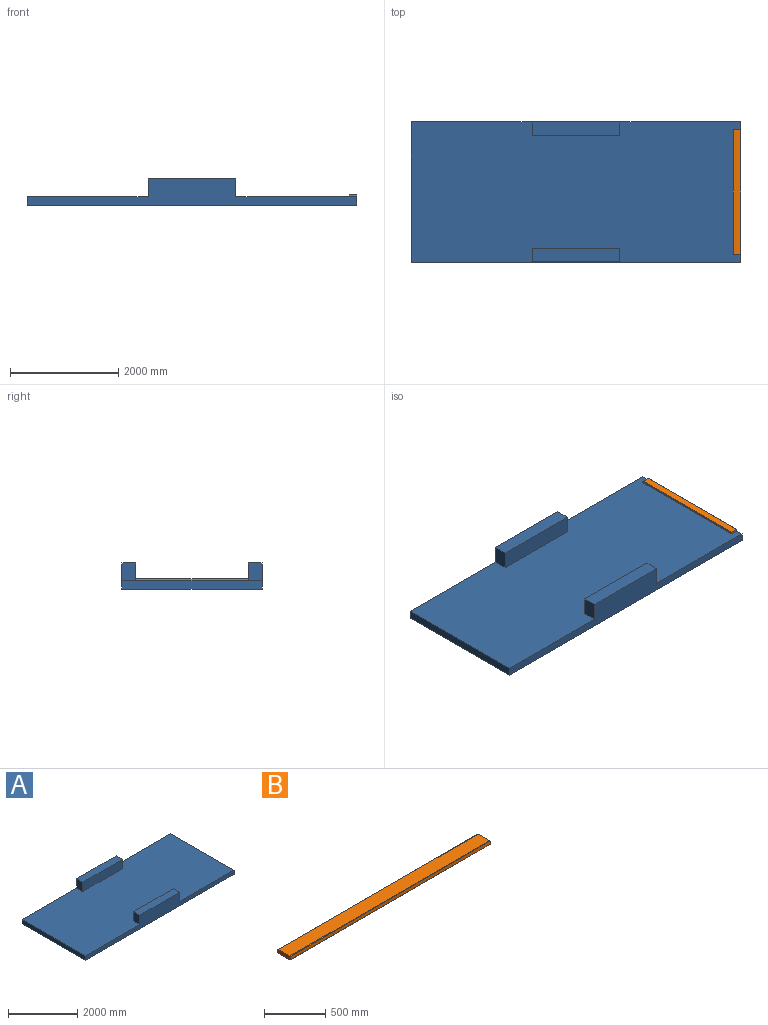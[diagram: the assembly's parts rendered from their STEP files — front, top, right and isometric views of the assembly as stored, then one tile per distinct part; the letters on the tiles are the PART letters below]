
ASSEMBLY  parts=2 mates=2
PART A: 14 faces, bbox 6096x2590.8x482.6 mm
  f0: plane 6096x2590.8mm, normal (0,0,1), area 14967712mm2, adj f1,f2,f3,f4,f6,f7,f8,f10
  f1: plane 2590.8x152.4mm, normal (1,0,0), area 394837.9mm2, adj f0,f2,f4,f5
  f2: plane 6096x482.6mm, normal (0,1,0), area 1465803.5mm2, adj f0,f1,f3,f5,f10,f12,f13
  f3: plane 2590.8x152.4mm, normal (-1,0,0), area 394837.9mm2, adj f0,f2,f4,f5
  f4: plane 6096x482.6mm, normal (0,-1,0), area 1465803.5mm2, adj f0,f1,f3,f5,f6,f8,f9
  f5: plane 6096x2590.8mm, normal (0,0,-1), area 15793516.8mm2, adj f1,f2,f3,f4
  f6: plane 330.2x254mm, normal (1,0,0), area 83870.8mm2, adj f0,f4,f7,f9
  f7: plane 1625.6x330.2mm, normal (0,1,0), area 536773.1mm2, adj f0,f6,f8,f9
  f8: plane 330.2x254mm, normal (-1,0,0), area 83870.8mm2, adj f0,f4,f7,f9
  f9: plane 1625.6x254mm, normal (0,0,1), area 412902.4mm2, adj f4,f6,f7,f8
  f10: plane 330.2x254mm, normal (-1,0,0), area 83870.8mm2, adj f0,f2,f11,f13
  f11: plane 1625.6x330.2mm, normal (0,-1,0), area 536773.1mm2, adj f0,f10,f12,f13
  f12: plane 330.2x254mm, normal (1,0,0), area 83870.8mm2, adj f0,f2,f11,f13
  f13: plane 1625.6x254mm, normal (0,0,1), area 412902.4mm2, adj f2,f10,f11,f12
PART B: 10 faces, bbox 2311.4x139.7x38.1 mm
  f0: plane 2311.4x31.75mm, normal (0,-1,0), area 73386.9mm2, adj f1,f7,f8,f9
  f1: cylinder r=3.17mm len=2311.4mm, axis (-1,0,0), area 11527.6mm2, adj f0,f2,f8,f9
  f2: plane 2311.4x133.35mm, normal (0,0,-1), area 308225.2mm2, adj f1,f3,f8,f9
  f3: cylinder r=3.17mm len=2311.4mm, axis (-1,0,0), area 11527.6mm2, adj f2,f4,f8,f9
  f4: plane 2311.4x31.75mm, normal (0,1,0), area 73386.9mm2, adj f3,f5,f8,f9
  f5: cylinder r=3.17mm len=2311.4mm, axis (-1,0,0), area 11527.6mm2, adj f4,f6,f8,f9
  f6: plane 2311.4x133.35mm, normal (0,0,1), area 308225.2mm2, adj f5,f7,f8,f9
  f7: cylinder r=3.17mm len=2311.4mm, axis (-1,0,0), area 11527.6mm2, adj f0,f6,f8,f9
  f8: plane 139.7x38.1mm, normal (1,0,0), area 5313.9mm2, adj f0,f1,f2,f3,f4,f5,f6,f7
  f9: plane 139.7x38.1mm, normal (-1,0,0), area 5313.9mm2, adj f0,f1,f2,f3,f4,f5,f6,f7
PLACE A rot(axis=(0,0,1),180deg) t=(-2945.03,0,0)mm
PLACE B rot(axis=(0,0,1),90deg) t=(33.12,0,19.05)mm
MATE planar B.f0 <-> A.f3  axis (1,0,0) through (102.97,0,19.05)mm
MATE planar B.f2 <-> A.f0  axis (0,0,-1) through (33.12,0,0)mm
